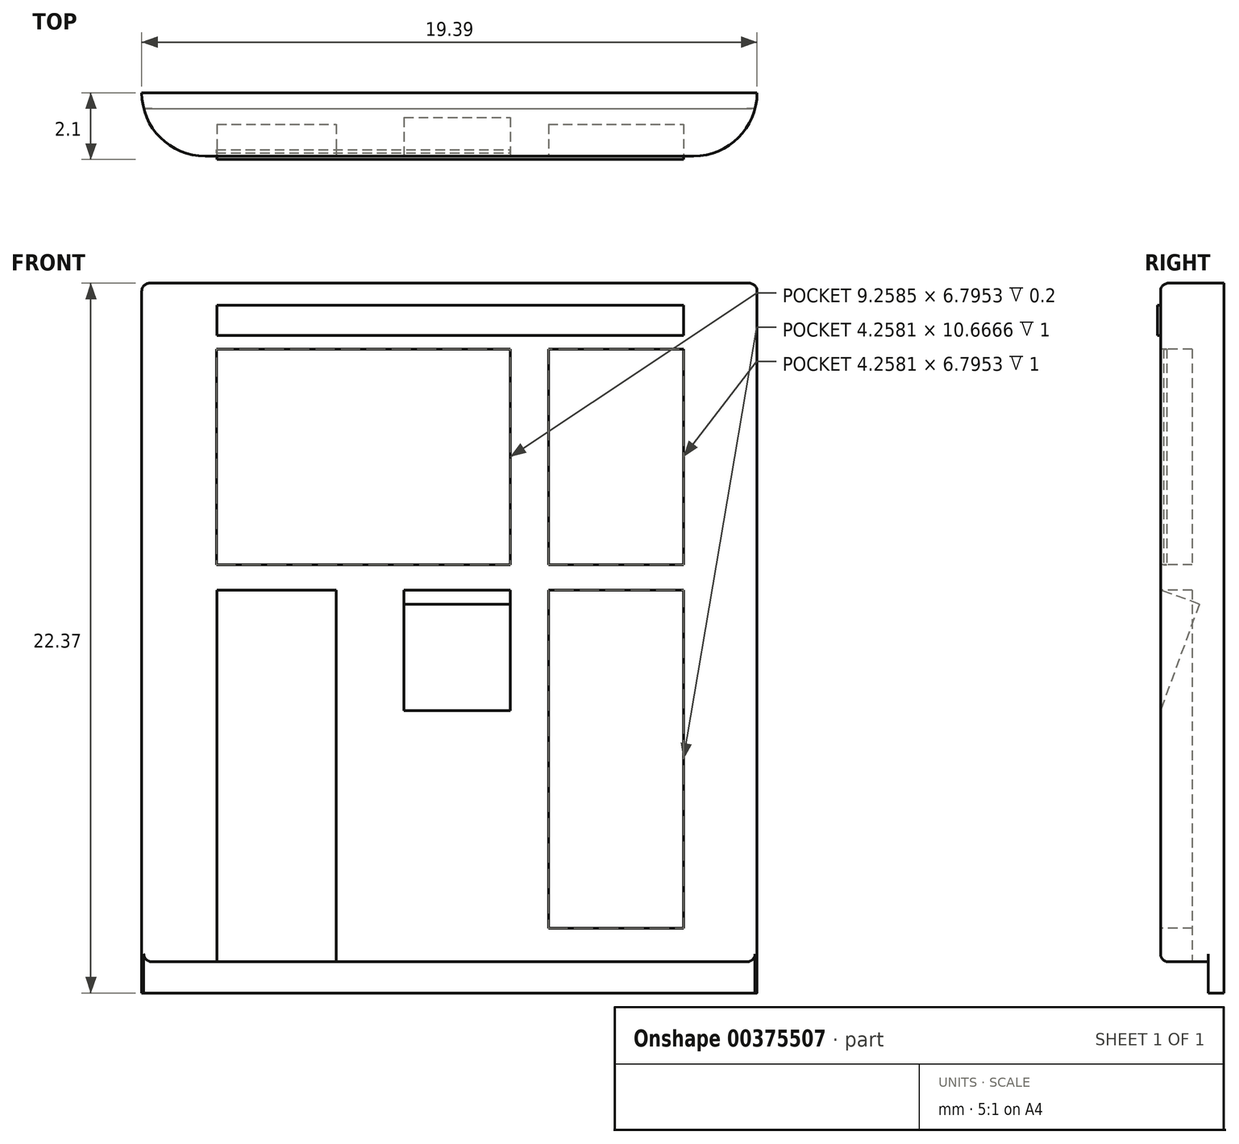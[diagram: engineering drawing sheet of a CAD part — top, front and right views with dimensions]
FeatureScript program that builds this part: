
annotation { "Feature Type Name" : "Feature", "Feature Type Description" : "" }
export const myFeature = defineFeature(function(context is Context, id is Id, definition is map)
    precondition{}
    {
        {
            var Q0;
            Q0=qCreatedBy(makeId("Front.planeOp"),FACE);
            var sketch = newSketch(context, id + "F0", { "sketchPlane" : qUnion([Q0])});
            skLineSegment(sketch, "E0.bottom", {"start": v(0, 22.37) * mm, "end": v(19.4, 22.37) * mm});
            skLineSegment(sketch, "E0.top", {"start": v(0, 0) * mm, "end": v(19.4, 0) * mm});
            skLineSegment(sketch, "E0.left", {"start": v(0, 22.37) * mm, "end": v(0, 0) * mm});
            skLineSegment(sketch, "E0.right", {"start": v(19.4, 22.37) * mm, "end": v(19.4, 0) * mm});
            skLineSegment(sketch, "E1", {"start": v(0, 0.98) * mm, "end": v(19.4, 0.98) * mm});
            skSolve(sketch);
        }
        {
            var Q0;
            {var subQ0=sQuery(id+"F0.wireOp",EDGE,"E0.bottom");Q0=makeQuery(id+"F0.imprint","IMPRINT",FACE,{"disambiguationData":[TD([[makeQuery(id+"F0.imprint","IMPRINT",EDGE,{"derivedFrom":subQ0}),-1.0]])]});}
            extrude(context, id + "F1", {"entities" : qUnion([Q0]), "depth" : 2 * mm});
        }
        {
            var Q0;
            {var subQ0=sQuery(id+"F0.wireOp",EDGE,"E0.top");Q0=makeQuery(id+"F0.imprint","IMPRINT",FACE,{"disambiguationData":[TD([[makeQuery(id+"F0.imprint","IMPRINT",EDGE,{"derivedFrom":subQ0}),1.0]])]});}
            extrude(context, id + "F2", {"entities" : qUnion([Q0]), "operationType" : NewBodyOperationType.ADD, "depth" : 0.5 * mm});
        }
        {
            var Q0;
            Q0=makeQuery(id+"F1.opExtrude","CAP_EDGE",EDGE,{"disambiguationData":[OSD([sQuery(id+"F0.wireOp",EDGE,"E0.left")])],"isStart":false});
            var Q1;
            Q1=makeQuery(id+"F1.opExtrude","CAP_EDGE",EDGE,{"disambiguationData":[OSD([sQuery(id+"F0.wireOp",EDGE,"E0.right")])],"isStart":false});
            fillet(context, id + "F3", {"entities" : qUnion([Q0, Q1]), "radius" : 2 * mm, "tangentPropagation" : true, "allowEdgeOverflow" : false});
        }
        {
            var Q0;
            Q0=makeQuery(id+"F1.opExtrude","CAP_EDGE",EDGE,{"disambiguationData":[OSD([sQuery(id+"F0.wireOp",EDGE,"E0.bottom")])],"isStart":false});
            var Q1;
            Q1=makeQuery(id+"F1.opExtrude","CAP_EDGE",EDGE,{"disambiguationData":[OSD([sQuery(id+"F0.wireOp",EDGE,"E1")])],"isStart":false});
            fillet(context, id + "F4", {"entities" : qUnion([Q0, Q1]), "radius" : .25 * mm, "tangentPropagation" : true, "allowEdgeOverflow" : false});
        }
        {
            var Q0;
            Q0=makeQuery(id+"F1.opExtrude","CAP_FACE",FACE,{"disambiguationData":[OSD([sQuery(id+"F0.wireOp",EDGE,"E0.bottom"),sQuery(id+"F0.wireOp",EDGE,"E0.left"),sQuery(id+"F0.wireOp",EDGE,"E0.right"),sQuery(id+"F0.wireOp",EDGE,"E1")])],"isStart":false});
            var sketch = newSketch(context, id + "F5", { "sketchPlane" : qUnion([Q0])});
            skLineSegment(sketch, "E2.bottom", {"start": v(2.36, 21.67) * mm, "end": v(17.07, 21.67) * mm});
            skLineSegment(sketch, "E2.top", {"start": v(2.36, 20.72) * mm, "end": v(17.07, 20.72) * mm});
            skLineSegment(sketch, "E2.left", {"start": v(2.36, 21.67) * mm, "end": v(2.36, 20.72) * mm});
            skLineSegment(sketch, "E2.right", {"start": v(17.07, 21.67) * mm, "end": v(17.07, 20.72) * mm});
            skSolve(sketch);
        }
        {
            var Q0;
            Q0=makeQuery(id+"F5.imprint","IMPRINT",FACE,{"disambiguationData":[TD([[makeQuery(id+"F5.imprint","IMPRINT",EDGE,{"derivedFrom":sQuery(id+"F5.wireOp",EDGE,"E2.bottom")}),-1.0]])]});
            extrude(context, id + "F6", {"entities" : qUnion([Q0]), "depth" : .1 * mm});
        }
        {
            var Q0;
            Q0=makeQuery(id+"F1.opExtrude","CAP_FACE",FACE,{"disambiguationData":[OSD([sQuery(id+"F0.wireOp",EDGE,"E0.bottom"),sQuery(id+"F0.wireOp",EDGE,"E0.left"),sQuery(id+"F0.wireOp",EDGE,"E0.right"),sQuery(id+"F0.wireOp",EDGE,"E1")])],"isStart":false});
            var sketch = newSketch(context, id + "F7", { "sketchPlane" : qUnion([Q0])});
            skLineSegment(sketch, "E3.bottom", {"start": v(2.35, 20.3) * mm, "end": v(11.61, 20.3) * mm});
            skLineSegment(sketch, "E3.top", {"start": v(2.35, 13.5) * mm, "end": v(11.61, 13.5) * mm});
            skLineSegment(sketch, "E3.left", {"start": v(2.35, 20.3) * mm, "end": v(2.35, 13.5) * mm});
            skLineSegment(sketch, "E3.right", {"start": v(11.61, 20.3) * mm, "end": v(11.61, 13.5) * mm});
            skSolve(sketch);
        }
        {
            var Q0;
            Q0=makeQuery(id+"F7.imprint","IMPRINT",FACE,{"disambiguationData":[TD([[makeQuery(id+"F7.imprint","IMPRINT",EDGE,{"derivedFrom":sQuery(id+"F7.wireOp",EDGE,"E3.bottom")}),-1.0]])]});
            extrude(context, id + "F8", {"entities" : qUnion([Q0]), "operationType" : NewBodyOperationType.REMOVE, "oppositeDirection" : true, "depth" : .2 * mm});
        }
        {
            var Q0;
            Q0=makeQuery(id+"F8.boolean.opBoolean","COPY",FACE,{"derivedFrom":makeQuery(id+"F8.opExtrude","CAP_FACE",FACE,{"disambiguationData":[OSD([sQuery(id+"F7.wireOp",EDGE,"E3.bottom"),sQuery(id+"F7.wireOp",EDGE,"E3.top"),sQuery(id+"F7.wireOp",EDGE,"E3.left"),sQuery(id+"F7.wireOp",EDGE,"E3.right")])],"isStart":false})});
            extrude(context, id + "F9", {"entities" : qUnion([Q0]), "depth" : .1 * mm});
        }
        {
            var Q0;
            Q0=makeQuery(id+"F1.opExtrude","CAP_FACE",FACE,{"disambiguationData":[OSD([sQuery(id+"F0.wireOp",EDGE,"E0.bottom"),sQuery(id+"F0.wireOp",EDGE,"E0.left"),sQuery(id+"F0.wireOp",EDGE,"E0.right"),sQuery(id+"F0.wireOp",EDGE,"E1")])],"isStart":false});
            var sketch = newSketch(context, id + "F10", { "sketchPlane" : qUnion([Q0])});
            skLineSegment(sketch, "E4.bottom", {"start": v(12.82, 20.3) * mm, "end": v(17.07, 20.3) * mm});
            skLineSegment(sketch, "E4.top", {"start": v(12.82, 13.5) * mm, "end": v(17.07, 13.5) * mm});
            skLineSegment(sketch, "E4.left", {"start": v(12.82, 20.3) * mm, "end": v(12.82, 13.5) * mm});
            skLineSegment(sketch, "E4.right", {"start": v(17.07, 20.3) * mm, "end": v(17.07, 13.5) * mm});
            skLineSegment(sketch, "E5.bottom", {"start": v(2.37, 12.7) * mm, "end": v(6.12, 12.7) * mm});
            skLineSegment(sketch, "E5.top", {"start": v(2.37, 0.67) * mm, "end": v(6.12, 0.67) * mm});
            skLineSegment(sketch, "E5.left", {"start": v(2.37, 12.7) * mm, "end": v(2.37, 0.67) * mm});
            skLineSegment(sketch, "E5.right", {"start": v(6.12, 12.7) * mm, "end": v(6.12, 0.67) * mm});
            skLineSegment(sketch, "E6.bottom", {"start": v(12.82, 12.7) * mm, "end": v(17.07, 12.7) * mm});
            skLineSegment(sketch, "E6.top", {"start": v(12.82, 2.03) * mm, "end": v(17.07, 2.03) * mm});
            skLineSegment(sketch, "E6.left", {"start": v(12.82, 12.7) * mm, "end": v(12.82, 2.03) * mm});
            skLineSegment(sketch, "E6.right", {"start": v(17.07, 12.7) * mm, "end": v(17.07, 2.03) * mm});
            skSolve(sketch);
        }
        {
            var Q0;
            Q0=makeQuery(id+"F10.imprint","IMPRINT",FACE,{"disambiguationData":[TD([[makeQuery(id+"F10.imprint","IMPRINT",EDGE,{"derivedFrom":sQuery(id+"F10.wireOp",EDGE,"E4.bottom")}),-1.0]])]});
            var Q1;
            {var subQ0=sQuery(id+"F10.wireOp",EDGE,"E6.bottom");Q1=makeQuery(id+"F10.imprint","IMPRINT",FACE,{"disambiguationData":[TD([[makeQuery(id+"F10.imprint","IMPRINT",EDGE,{"derivedFrom":subQ0}),-1.0]])]});}
            var Q2;
            {var subQ0=sQuery(id+"F10.wireOp",EDGE,"E5.bottom");Q2=makeQuery(id+"F10.imprint","IMPRINT",FACE,{"disambiguationData":[TD([[makeQuery(id+"F10.imprint","IMPRINT",EDGE,{"derivedFrom":subQ0}),-1.0]])]});}
            var Q3;
            {var subQ0=sQuery(id+"F10.wireOp",EDGE,"E5.top");Q3=makeQuery(id+"F10.imprint","IMPRINT",FACE,{"disambiguationData":[TD([[makeQuery(id+"F10.imprint","IMPRINT",EDGE,{"derivedFrom":subQ0}),1.0]])]});}
            var Q4;
            {var subQ0=sQuery(id+"F10.wireOp",EDGE,"E6.top");Q4=makeQuery(id+"F10.imprint","IMPRINT",FACE,{"disambiguationData":[TD([[makeQuery(id+"F10.imprint","IMPRINT",EDGE,{"derivedFrom":subQ0}),1.0]])]});}
            extrude(context, id + "F11", {"entities" : qUnion([Q0, Q1, Q2, Q3, Q4]), "operationType" : NewBodyOperationType.REMOVE, "oppositeDirection" : true, "depth" : 1 * mm});
        }
        {
            var Q0;
            Q0=makeQuery(id+"F1.opExtrude","CAP_FACE",FACE,{"disambiguationData":[OSD([sQuery(id+"F0.wireOp",EDGE,"E0.bottom"),sQuery(id+"F0.wireOp",EDGE,"E0.left"),sQuery(id+"F0.wireOp",EDGE,"E0.right"),sQuery(id+"F0.wireOp",EDGE,"E1")])],"isStart":false});
            var sketch = newSketch(context, id + "F12", { "sketchPlane" : qUnion([Q0])});
            skLineSegment(sketch, "E7", {"start": v(6.96, 12.7) * mm, "end": v(11.97, 12.7) * mm, "construction": true});
            skSolve(sketch);
        }
        {
            var Q0;
            Q0=sQuery(id+"F12.wireOp",EDGE,"E7");
            cPlane(context, id + "F13", {"entities" : qUnion([Q0]), "cplaneType" : CPlaneType.LINE_ANGLE, "offset" : 25 * mm, "angle" : 20 * degree, "oppositeDirection" : true, "width" : 150 * mm, "height" : 150 * mm});
        }
        {
            var Q0;
            Q0=qCreatedBy(id+"F13.planeOp",FACE);
            var sketch = newSketch(context, id + "F14", { "sketchPlane" : qUnion([Q0])});
            skLineSegment(sketch, "E8.bottom", {"start": v(-8.27, 11.25) * mm, "end": v(-11.61, 11.25) * mm});
            skLineSegment(sketch, "E8.top", {"start": v(-8.27, 7.29) * mm, "end": v(-11.61, 7.29) * mm});
            skLineSegment(sketch, "E8.left", {"start": v(-8.27, 11.25) * mm, "end": v(-8.27, 7.29) * mm});
            skLineSegment(sketch, "E8.right", {"start": v(-11.61, 11.25) * mm, "end": v(-11.61, 7.29) * mm});
            skSolve(sketch);
        }
        {
            var Q0;
            Q0 = qSketchRegion(id + "F14", true);
            extrude(context, id + "F15", {"entities" : qUnion([Q0]), "operationType" : NewBodyOperationType.REMOVE, "depth" : 1.3 * mm});
        }
    });
